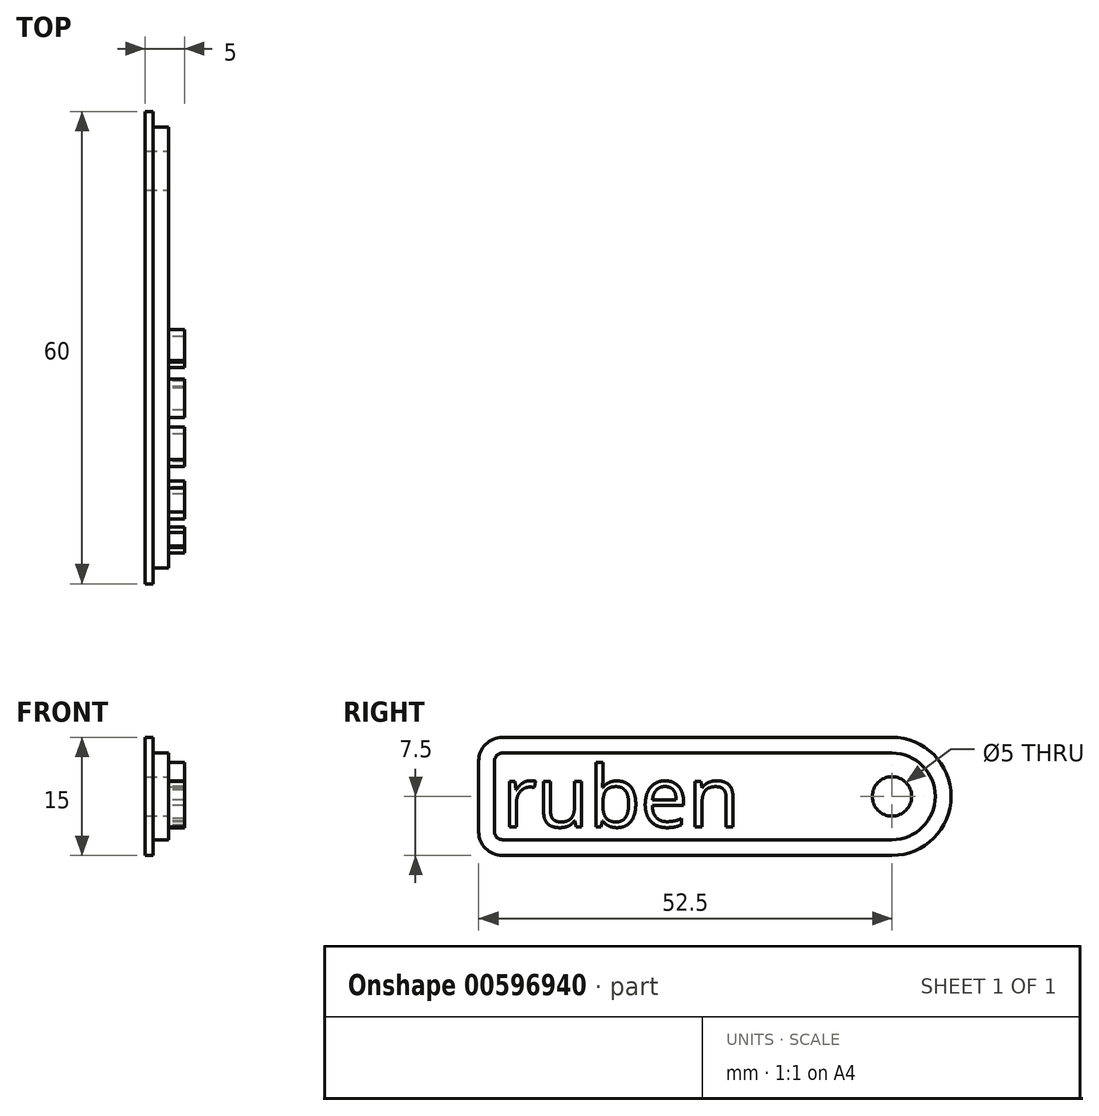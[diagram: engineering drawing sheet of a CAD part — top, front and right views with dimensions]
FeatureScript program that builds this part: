
annotation { "Feature Type Name" : "Feature", "Feature Type Description" : "" }
export const myFeature = defineFeature(function(context is Context, id is Id, definition is map)
    precondition{}
    {
        {
            var Q0;
            Q0=qCreatedBy(makeId("Right.planeOp"),FACE);
            var sketch = newSketch(context, id + "F0", { "sketchPlane" : qUnion([Q0])});
            skLineSegment(sketch, "E0.bottom", {"start": v(4.5, 30) * mm, "end": v(-4.5, 30) * mm});
            skLineSegment(sketch, "E0.left", {"start": v(7.5, 27) * mm, "end": v(7.5, -22.5) * mm});
            skLineSegment(sketch, "E0.right", {"start": v(-7.5, 27) * mm, "end": v(-7.5, -22.5) * mm});
            skPoint(sketch, "E1.visualSharp", {"position": v(7.5, 30) * mm});
            skArc(sketch, "E1.filletArc", {"start": v(7.5, 27) * mm, "mid": v(6.62, 29.12) * mm, "end": v(4.5, 30) * mm});
            skPoint(sketch, "E2.visualSharp", {"position": v(-7.5, 30) * mm});
            skArc(sketch, "E2.filletArc", {"start": v(-4.5, 30) * mm, "mid": v(-6.62, 29.12) * mm, "end": v(-7.5, 27) * mm});
            skArc(sketch, "E3", {"start": v(-7.5, -22.5) * mm, "mid": v(0, -30) * mm, "end": v(7.5, -22.5) * mm});
            skLineSegment(sketch, "E4", {"start": v(9.64, -30) * mm, "end": v(-13.5, -30) * mm, "construction": true});
            skCircle(sketch, "E5", {"center": v(0, -22.5) * mm, "radius": 2.5 * mm});
            skSolve(sketch);
        }
        {
            var Q0;
            Q0 = qSketchRegion(id + "F0", true);
            extrude(context, id + "F1", {"entities" : qUnion([Q0]), "oppositeDirection" : true, "depth" : 3 * mm, "offsetDistance" : 25 * mm});
        }
        {
            var Q0;
            Q0=makeQuery(id+"F1.opExtrude","CAP_FACE",FACE,{"disambiguationData":[OSD([sQuery(id+"F0.wireOp",EDGE,"E0.bottom"),sQuery(id+"F0.wireOp",EDGE,"E0.left"),sQuery(id+"F0.wireOp",EDGE,"E0.right"),sQuery(id+"F0.wireOp",EDGE,"E1.filletArc"),sQuery(id+"F0.wireOp",EDGE,"E2.filletArc"),sQuery(id+"F0.wireOp",EDGE,"E3"),sQuery(id+"F0.wireOp",EDGE,"E5")])],"isStart":true});
            var sketch = newSketch(context, id + "F2", { "sketchPlane" : qUnion([Q0])});
            skPoint(sketch, "E6", {"position": v(0, 0) * mm});
            skCircle(sketch, "E7", {"center": v(0, 0) * mm, "radius": 5.67 * mm});
            skSolve(sketch);
        }
        {
            var Q0;
            Q0=makeQuery(id+"F1.opExtrude","SWEPT_BODY",BODY,{"disambiguationData":[OSD([sQuery(id+"F0.wireOp",EDGE,"E0.bottom"),sQuery(id+"F0.wireOp",EDGE,"E0.left"),sQuery(id+"F0.wireOp",EDGE,"E0.right"),sQuery(id+"F0.wireOp",EDGE,"E1.filletArc"),sQuery(id+"F0.wireOp",EDGE,"E2.filletArc"),sQuery(id+"F0.wireOp",EDGE,"E3"),sQuery(id+"F0.wireOp",EDGE,"E5")])]});
            var Q1;
            Q1=sQuery(id+"F2.wireOp",EDGE,"E7");
            transform(context, id + "F3", {"entities" : qUnion([Q0]), "transformType" : TransformType.ROTATION, "transformAxis" : qUnion([Q1]), "angle" : 90 * degree, "makeCopy" : false});
        }
        {
            var Q0;
            Q0=makeQuery(id+"F1.opExtrude","CAP_FACE",FACE,{"disambiguationData":[OSD([sQuery(id+"F0.wireOp",EDGE,"E0.bottom"),sQuery(id+"F0.wireOp",EDGE,"E0.left"),sQuery(id+"F0.wireOp",EDGE,"E0.right"),sQuery(id+"F0.wireOp",EDGE,"E1.filletArc"),sQuery(id+"F0.wireOp",EDGE,"E2.filletArc"),sQuery(id+"F0.wireOp",EDGE,"E3"),sQuery(id+"F0.wireOp",EDGE,"E5")])],"isStart":true});
            var sketch = newSketch(context, id + "F4", { "sketchPlane" : qUnion([Q0])});
            skText(sketch, "E8", { "text": "ruben", "fontName": "OpenSans-Regular.ttf"});
            const initialGuessF4  = {"E8": [-0.027, -0.00387, 1, 0, 0.00773]};
            skSetInitialGuess(sketch, initialGuessF4);
            skSolve(sketch);
        }
        {
            var Q0;
            Q0 = qSketchRegion(id + "F4", true);
            extrude(context, id + "F5", {"entities" : qUnion([Q0]), "operationType" : NewBodyOperationType.ADD, "depth" : 2 * mm, "offsetDistance" : 25 * mm});
        }
        {
            var Q0;
            Q0=makeQuery(id+"F4.imprint","IMPRINT",FACE,{"disambiguationData":[TD([[makeQuery(id+"F4.imprint","IMPRINT",EDGE,{"derivedFrom":sQuery(id+"F4.wireOp",EDGE,"E8.sketch_text.stroke-0")}),1.0]])]});
            var sketch = newSketch(context, id + "F6", { "sketchPlane" : qUnion([Q0])});
            skArc(sketch, "E9.0", {"start": v(-27, 5.5) * mm, "mid": v(-27.7, 5.2) * mm, "end": v(-28, 4.5) * mm});
            skArc(sketch, "E9.1", {"start": v(22.5, -5.5) * mm, "mid": v(28, 0) * mm, "end": v(22.5, 5.5) * mm});
            skLineSegment(sketch, "E9.2", {"start": v(-27, -5.5) * mm, "end": v(22.5, -5.5) * mm});
            skLineSegment(sketch, "E9.3", {"start": v(-27, 5.5) * mm, "end": v(22.5, 5.5) * mm});
            skArc(sketch, "E9.4", {"start": v(-28, -4.5) * mm, "mid": v(-27.7, -5.2) * mm, "end": v(-27, -5.5) * mm});
            skLineSegment(sketch, "E9.5", {"start": v(-28, 4.5) * mm, "end": v(-28, -4.5) * mm});
            skLineSegment(sketch, "E10.0", {"start": v(-27, 7.5) * mm, "end": v(22.5, 7.5) * mm});
            skArc(sketch, "E11.0", {"start": v(22.5, -7.5) * mm, "mid": v(30, 0) * mm, "end": v(22.5, 7.5) * mm});
            skLineSegment(sketch, "E12.0", {"start": v(-27, -7.5) * mm, "end": v(22.5, -7.5) * mm});
            skLineSegment(sketch, "E13.0", {"start": v(-30, 4.5) * mm, "end": v(-30, -4.5) * mm});
            skPoint(sketch, "E14.0", {"position": v(-29.12, -6.62) * mm});
            skArc(sketch, "E15.0", {"start": v(-30, -4.5) * mm, "mid": v(-29.12, -6.62) * mm, "end": v(-27, -7.5) * mm});
            skPoint(sketch, "E16.0", {"position": v(-29.12, 6.62) * mm});
            skArc(sketch, "E17.0", {"start": v(-27, 7.5) * mm, "mid": v(-29.12, 6.62) * mm, "end": v(-30, 4.5) * mm});
            skSolve(sketch);
        }
        {
            var Q0;
            Q0=makeQuery(id+"F6.imprint","IMPRINT",FACE,{"disambiguationData":[TD([[makeQuery(id+"F6.imprint","IMPRINT",EDGE,{"derivedFrom":sQuery(id+"F6.wireOp",EDGE,"E9.0")}),-1.0]])]});
            extrude(context, id + "F7", {"entities" : qUnion([Q0]), "operationType" : NewBodyOperationType.REMOVE, "oppositeDirection" : true, "depth" : 2 * mm, "offsetDistance" : 25 * mm});
        }
    });
